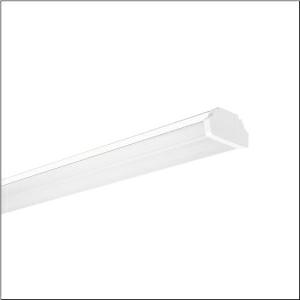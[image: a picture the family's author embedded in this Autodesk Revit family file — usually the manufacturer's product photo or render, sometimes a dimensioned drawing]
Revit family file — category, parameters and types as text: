
# Revit family: dus_r__31_ho_53bd812c1v6105_6b08
name_source: partatom
category: Lighting Fixtures
units: mm (PartAtom-declared; Revit-internal decimal feet)

## family parameters
Cut with Voids When Loaded = No
Host = Face
Light Source = No
Part Type = Normal
Room Calculation Point = No
Round Connector Dimension = Use Diameter
Shared = No

## types (1)
- --- (1 x LED, 10560 lm, 63.8 W, 6500K)
    Apparent Load = 64 VA
    CIE Flux Codes = 47 80 95 92 100
    Color Rendering = 80
    Color Temperature = 6500K
    Default Elevation = 1800 mm
    Description = DUS® 31 HO, luminaire insert, of sheet steel, coil coated, white, length: 1.535mm, width: 81mm, height: 90mm, 5x system unit, system units: 307mm, LED rated luminous flux: 10.560lm, light colour: 865, control gear: ON/OFF Multilumen, CLOi, control gear: ECG Multilumen, with plug, 3-pole, with phase selection, mains connection: 220..240V, AC, 50/60Hz, start of lifetime: 64W, end of service life: 73W, through-wiring accessed according to module size, primary optical cover: cover, of PMMA, light emission: direct distribution, primary light characteristic: symmetric, protection rating (complete): IP20, protection rating (LED compartment): IP50, insulation class (complete): insulation class I (protective earthing), certification: CE, ENEC, VDE, UKCA, impact resistance: IK03, permissible ambient temperature for indoor applications: -35..+35°C, corresponds to IFS (International Featured Standards) requirements for safety and quality in the food industry, reducing of maximum allowable ambient temperature of 5°C with ceiling mounting, packaging unit: 1 piece
    Height = 95 mm
    Lamp = 1 x LED
    Lamp Light Flux = 10560 lm
    Lamp Power = 63.8 W
    Lamp count = 1
    Length = 1535 mm
    Luminous efficacy = 166 lm/W
    Manufacturer = Siteco
    ModVariant = No
    Model = 53BD812C1V6105
    Mounting Place = Ceiling
    Mounting Type = Pendant
    Number of Poles = 1
    OnlyDefault = Yes
    Power Factor = 1
    Product Name = DUS® 31 HO
    Product group = luminaire insert
    ProductGroupID = 901
    Protection Class = Protection class I
    Protection Degree = IP 20
    RLX_Detail_Level = 1
    RLX_Emergency_Light_Flux = 0 lm
    RLX_Emergency_Type = 0
    RLX_Emergency_Type_DB = No
    RlxData = <blob elided: 39925 chars, md5=7ce9b8eb>
    Socket = socket
    Standby Power = 0 W
    System Light Flux = 10560 lm
    System Power = 64 W
    Type Comments = factory setting: luminous flux: 100 % | (A | C | E) | 144 mA
    Type Image = l_1003451.jpg
    URL = http://relux.com
    VarID = @adj_138079
    Voltage = 0 V
    Weight = 0.00 kg
    Width = 81 mm

## geometry (parser evidence)
native form markers: Blend x4, Sweep x11
no freeform markers — native parametric forms only
